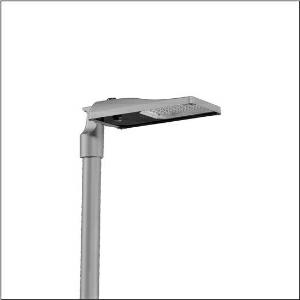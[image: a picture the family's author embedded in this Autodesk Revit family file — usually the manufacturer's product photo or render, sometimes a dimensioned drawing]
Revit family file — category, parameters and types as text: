
# Revit family: streetlight_sl_31_mini___p0_8a_5xh2u4at08ja_add1
name_source: partatom
category: Lighting Fixtures
units: mm (PartAtom-declared; Revit-internal decimal feet)

## family parameters
Cut with Voids When Loaded = No
Host = Face
Light Source = No
Part Type = Normal
Room Calculation Point = No
Round Connector Dimension = Use Diameter
Shared = No

## types (1)
- --- (1 x LED, 12820 lm, 82.5 W, 4000K)
    Apparent Load = 83 VA
    CIE Flux Codes = 36 69 97 100 100
    Color Rendering = 70
    Color Temperature = 4000K
    Default Elevation = 1800 mm
    Description = Streetlight SL 31 mini D4i mast luminaire for post-top, side-entry; light control with lens of PMMA; light distribution: P0.8a, direct asymmetric distribution, for standard-compliant lighting for roads and squares; LED: luminous flux: 12.820lm, light colour: 740, colour temperature: 4000K; luminous efficacy: 155,4lm/W; control: pre-setting: logarithmic dimming characteristic, flexible luminous flux parameterisation, time-dependent luminous flux control, constant luminous flux control, power reduction, intelligent temperature release in ECG and LED module, overheat protection; luminaire housing, of diecast aluminium, SITECO metallic grey (DB 702S), corrosivity category C5 high according to DIN EN ISO 12944; cover of toughened safety glass, transparent, mast flange of diecast aluminium, SITECO metallic grey (DB 702S), spigot size: 76/60mm, mast flange included unmounted; cable length: 10,5m, connection cable pre-assembled; mains connection: 220..240V, AC, 50/60Hz; power consumption (at start of service life): 82,5W / (at end of service life): 90,1W / (with reduced operation 50%): 36,8W; protection rating (complete): IP66; insulation class (complete): insulation class II (safety insulation); impact resistance: IK09; certification: CE, ENEC, ENEC+, VDE, UKCA, ZD4i; permissible operating ambient temperature for outdoor applications: -40..+50°C; packaging unit: 1 piece

Light Distribution: P0.8a
    Height = 76 mm
    Lamp = 1 x LED
    Lamp Light Flux = 12820 lm
    Lamp Power = 82.5 W
    Lamp count = 1
    Length = 547 mm
    Luminous efficacy = 155 lm/W
    Manufacturer = Siteco
    ModVariant = No
    Model = 5XH2U4AT08JA
    Number of Poles = 1
    OnlyDefault = Yes
    Power Factor = 1
    Product Name = Streetlight SL 31 mini | P0.8a
    Product group = mast luminaire | pylon top
    ProductGroupID = 6100
    Protection Class = Protection class II
    Protection Degree = IP 66
    RLX_Detail_Level = 1
    RLX_Emergency_Light_Flux = 0 lm
    RLX_Emergency_Type = 0
    RLX_Emergency_Type_DB = No
    RlxData = <blob elided: 39609 chars, md5=3ce61df7>
    Socket = socket
    Standby Power = 0 W
    System Light Flux = 12820 lm
    System Power = 83 W
    Type Comments = factory setting: luminous flux: 100 % | dim-lin: 254 | 870 mA
    Type Image = l_1300332.jpg
    URL = http://relux.com
    VarID = @adj_065155
    Voltage = 0 V
    Weight = 0.00 kg
    Width = 265 mm

## geometry (parser evidence)
native form markers: Blend x4, Sweep x9
no freeform markers — native parametric forms only
